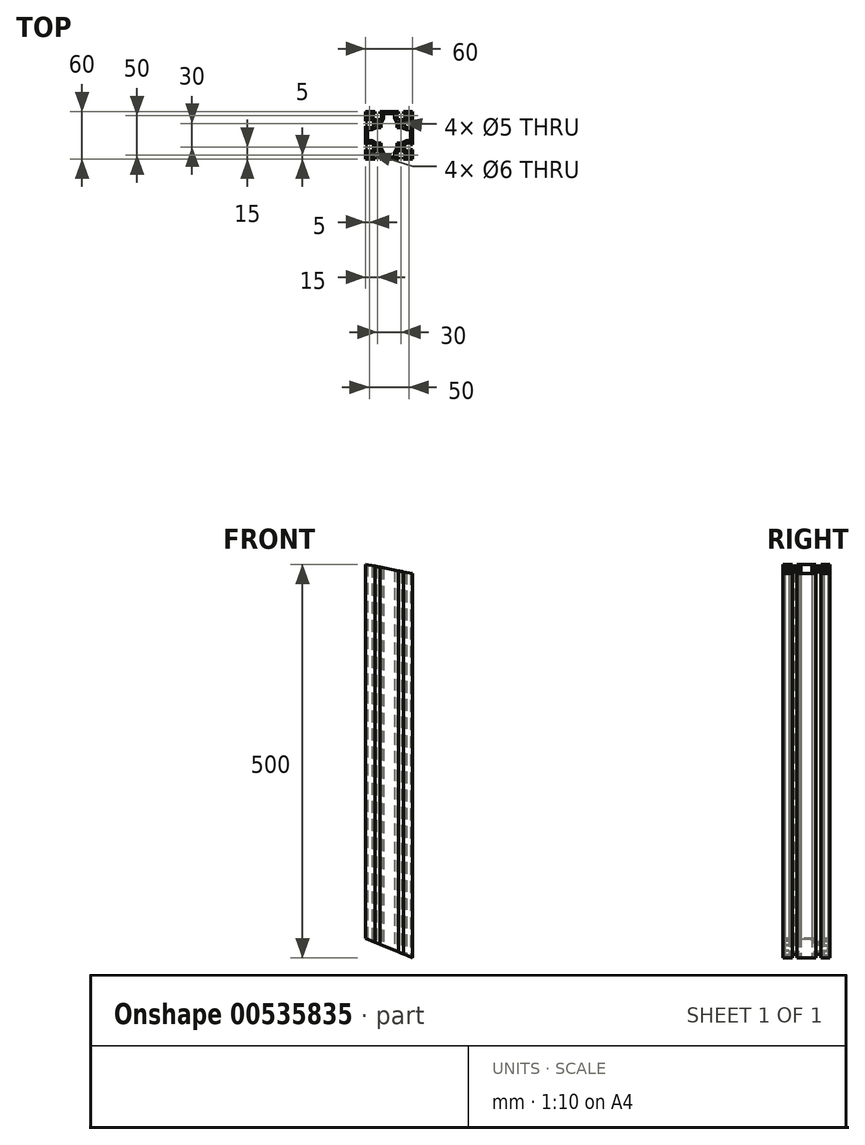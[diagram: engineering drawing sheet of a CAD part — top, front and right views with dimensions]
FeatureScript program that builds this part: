
annotation { "Feature Type Name" : "Feature", "Feature Type Description" : "" }
export const myFeature = defineFeature(function(context is Context, id is Id, definition is map)
    precondition{}
    {
        {
            var Q0;
            Q0=qCreatedBy(makeId("Top.planeOp"),FACE);
            var sketch = newSketch(context, id + "F0", { "sketchPlane" : qUnion([Q0])});
            skLineSegment(sketch, "E0.bottom", {"start": v(30, -30) * mm, "end": v(-30, -30) * mm});
            skLineSegment(sketch, "E0.top", {"start": v(30, 30) * mm, "end": v(-30, 30) * mm});
            skLineSegment(sketch, "E0.left", {"start": v(30, -30) * mm, "end": v(30, 30) * mm});
            skLineSegment(sketch, "E0.right", {"start": v(-30, -30) * mm, "end": v(-30, 30) * mm});
            skPoint(sketch, "E0.middle", {"position": v(0, 0) * mm});
            skLineSegment(sketch, "E1.top", {"start": v(-11.85, 30) * mm, "end": v(-18.15, 30) * mm});
            skLineSegment(sketch, "E1.left", {"start": v(-11.85, 27.5) * mm, "end": v(-11.85, 30) * mm});
            skLineSegment(sketch, "E1.right", {"start": v(-18.15, 27.5) * mm, "end": v(-18.15, 30) * mm});
            skPoint(sketch, "E1.middle", {"position": v(-15, 28.75) * mm});
            skLineSegment(sketch, "E2.bottom", {"start": v(-9.85, 27.5) * mm, "end": v(-11.85, 27.5) * mm});
            skLineSegment(sketch, "E2.left", {"start": v(-9.85, 27.5) * mm, "end": v(-9.85, 21.55) * mm});
            skLineSegment(sketch, "E2.right", {"start": v(-20.15, 27.5) * mm, "end": v(-20.15, 21.55) * mm});
            skPoint(sketch, "E2.middle", {"position": v(-15, 24.52) * mm});
            skArc(sketch, "E3", {"start": v(-20.15, 21.55) * mm, "mid": v(-15, 19.5) * mm, "end": v(-9.85, 21.55) * mm});
            skPoint(sketch, "E4.MirrorP", {"position": v(15, 24.52) * mm});
            skPoint(sketch, "E5.MirrorP", {"position": v(15, 28.75) * mm});
            skLineSegment(sketch, "E6.MirrorCS", {"start": v(11.85, 27.5) * mm, "end": v(11.85, 30) * mm});
            skLineSegment(sketch, "E7.MirrorCS", {"start": v(18.15, 27.5) * mm, "end": v(18.15, 30) * mm});
            skLineSegment(sketch, "E8.MirrorCS", {"start": v(9.85, 27.5) * mm, "end": v(11.85, 27.5) * mm});
            skLineSegment(sketch, "E9.MirrorCS", {"start": v(9.85, 27.5) * mm, "end": v(9.85, 21.55) * mm});
            skArc(sketch, "E10.MirrorCS", {"start": v(20.15, 21.55) * mm, "mid": v(15, 19.5) * mm, "end": v(9.85, 21.55) * mm});
            skLineSegment(sketch, "E11.MirrorCS", {"start": v(20.15, 27.5) * mm, "end": v(20.15, 21.55) * mm});
            skLineSegment(sketch, "E12.MirrorCS", {"start": v(11.85, 30) * mm, "end": v(18.15, 30) * mm});
            skLineSegment(sketch, "E13.1.0", {"start": v(27.5, 20.15) * mm, "end": v(21.55, 20.15) * mm});
            skLineSegment(sketch, "E13.1.1", {"start": v(27.5, 9.85) * mm, "end": v(21.55, 9.85) * mm});
            skArc(sketch, "E13.1.2", {"start": v(21.55, 20.15) * mm, "mid": v(19.5, 15) * mm, "end": v(21.55, 9.85) * mm});
            skLineSegment(sketch, "E13.1.3", {"start": v(27.5, -9.85) * mm, "end": v(21.55, -9.85) * mm});
            skLineSegment(sketch, "E13.1.4", {"start": v(27.5, -20.15) * mm, "end": v(21.55, -20.15) * mm});
            skPoint(sketch, "E13.1.5", {"position": v(28.75, 15) * mm});
            skPoint(sketch, "E13.1.6", {"position": v(28.75, -15) * mm});
            skArc(sketch, "E13.1.7", {"start": v(21.55, -20.15) * mm, "mid": v(19.5, -15) * mm, "end": v(21.55, -9.85) * mm});
            skPoint(sketch, "E13.1.8", {"position": v(24.52, -15) * mm});
            skPoint(sketch, "E13.1.9", {"position": v(24.52, 15) * mm});
            skLineSegment(sketch, "E13.1.10", {"start": v(27.5, 9.85) * mm, "end": v(27.5, 20.15) * mm});
            skLineSegment(sketch, "E13.1.11", {"start": v(27.5, -11.85) * mm, "end": v(27.5, -18.15) * mm});
            skLineSegment(sketch, "E13.1.12", {"start": v(30, 11.85) * mm, "end": v(30, 18.15) * mm});
            skLineSegment(sketch, "E13.1.13", {"start": v(30, -11.85) * mm, "end": v(30, -18.15) * mm});
            skLineSegment(sketch, "E13.1.14", {"start": v(27.5, 18.15) * mm, "end": v(30, 18.15) * mm});
            skLineSegment(sketch, "E13.1.15", {"start": v(27.5, 11.85) * mm, "end": v(30, 11.85) * mm});
            skLineSegment(sketch, "E13.1.16", {"start": v(27.5, 11.85) * mm, "end": v(27.5, 18.15) * mm});
            skLineSegment(sketch, "E13.1.17", {"start": v(27.5, -9.85) * mm, "end": v(27.5, -20.15) * mm});
            skLineSegment(sketch, "E13.1.18", {"start": v(27.5, -18.15) * mm, "end": v(30, -18.15) * mm});
            skLineSegment(sketch, "E13.1.19", {"start": v(27.5, -11.85) * mm, "end": v(30, -11.85) * mm});
            skLineSegment(sketch, "E13.2.0", {"start": v(20.15, -27.5) * mm, "end": v(20.15, -21.55) * mm});
            skLineSegment(sketch, "E13.2.1", {"start": v(9.85, -27.5) * mm, "end": v(9.85, -21.55) * mm});
            skArc(sketch, "E13.2.2", {"start": v(20.15, -21.55) * mm, "mid": v(15, -19.5) * mm, "end": v(9.85, -21.55) * mm});
            skLineSegment(sketch, "E13.2.3", {"start": v(-9.85, -27.5) * mm, "end": v(-9.85, -21.55) * mm});
            skLineSegment(sketch, "E13.2.4", {"start": v(-20.15, -27.5) * mm, "end": v(-20.15, -21.55) * mm});
            skPoint(sketch, "E13.2.5", {"position": v(15, -28.75) * mm});
            skPoint(sketch, "E13.2.6", {"position": v(-15, -28.75) * mm});
            skArc(sketch, "E13.2.7", {"start": v(-20.15, -21.55) * mm, "mid": v(-15, -19.5) * mm, "end": v(-9.85, -21.55) * mm});
            skPoint(sketch, "E13.2.8", {"position": v(-15, -24.52) * mm});
            skPoint(sketch, "E13.2.9", {"position": v(15, -24.52) * mm});
            skLineSegment(sketch, "E13.2.10", {"start": v(9.85, -27.5) * mm, "end": v(20.15, -27.5) * mm});
            skLineSegment(sketch, "E13.2.11", {"start": v(-11.85, -27.5) * mm, "end": v(-18.15, -27.5) * mm});
            skLineSegment(sketch, "E13.2.12", {"start": v(11.85, -30) * mm, "end": v(18.15, -30) * mm});
            skLineSegment(sketch, "E13.2.13", {"start": v(-11.85, -30) * mm, "end": v(-18.15, -30) * mm});
            skLineSegment(sketch, "E13.2.14", {"start": v(18.15, -27.5) * mm, "end": v(18.15, -30) * mm});
            skLineSegment(sketch, "E13.2.15", {"start": v(11.85, -27.5) * mm, "end": v(11.85, -30) * mm});
            skLineSegment(sketch, "E13.2.16", {"start": v(11.85, -27.5) * mm, "end": v(18.15, -27.5) * mm});
            skLineSegment(sketch, "E13.2.17", {"start": v(-9.85, -27.5) * mm, "end": v(-20.15, -27.5) * mm});
            skLineSegment(sketch, "E13.2.18", {"start": v(-18.15, -27.5) * mm, "end": v(-18.15, -30) * mm});
            skLineSegment(sketch, "E13.2.19", {"start": v(-11.85, -27.5) * mm, "end": v(-11.85, -30) * mm});
            skLineSegment(sketch, "E13.3.0", {"start": v(-27.5, -20.15) * mm, "end": v(-21.55, -20.15) * mm});
            skLineSegment(sketch, "E13.3.1", {"start": v(-27.5, -9.85) * mm, "end": v(-21.55, -9.85) * mm});
            skArc(sketch, "E13.3.2", {"start": v(-21.55, -20.15) * mm, "mid": v(-19.5, -15) * mm, "end": v(-21.55, -9.85) * mm});
            skLineSegment(sketch, "E13.3.3", {"start": v(-27.5, 9.85) * mm, "end": v(-21.55, 9.85) * mm});
            skLineSegment(sketch, "E13.3.4", {"start": v(-27.5, 20.15) * mm, "end": v(-21.55, 20.15) * mm});
            skPoint(sketch, "E13.3.5", {"position": v(-28.75, -15) * mm});
            skPoint(sketch, "E13.3.6", {"position": v(-28.75, 15) * mm});
            skArc(sketch, "E13.3.7", {"start": v(-21.55, 20.15) * mm, "mid": v(-19.5, 15) * mm, "end": v(-21.55, 9.85) * mm});
            skPoint(sketch, "E13.3.8", {"position": v(-24.52, 15) * mm});
            skPoint(sketch, "E13.3.9", {"position": v(-24.52, -15) * mm});
            skLineSegment(sketch, "E13.3.10", {"start": v(-27.5, -9.85) * mm, "end": v(-27.5, -20.15) * mm});
            skLineSegment(sketch, "E13.3.11", {"start": v(-27.5, 11.85) * mm, "end": v(-27.5, 18.15) * mm});
            skLineSegment(sketch, "E13.3.12", {"start": v(-30, -11.85) * mm, "end": v(-30, -18.15) * mm});
            skLineSegment(sketch, "E13.3.13", {"start": v(-30, 11.85) * mm, "end": v(-30, 18.15) * mm});
            skLineSegment(sketch, "E13.3.14", {"start": v(-27.5, -18.15) * mm, "end": v(-30, -18.15) * mm});
            skLineSegment(sketch, "E13.3.15", {"start": v(-27.5, -11.85) * mm, "end": v(-30, -11.85) * mm});
            skLineSegment(sketch, "E13.3.16", {"start": v(-27.5, -11.85) * mm, "end": v(-27.5, -18.15) * mm});
            skLineSegment(sketch, "E13.3.17", {"start": v(-27.5, 9.85) * mm, "end": v(-27.5, 20.15) * mm});
            skLineSegment(sketch, "E13.3.18", {"start": v(-27.5, 18.15) * mm, "end": v(-30, 18.15) * mm});
            skLineSegment(sketch, "E13.3.19", {"start": v(-27.5, 11.85) * mm, "end": v(-30, 11.85) * mm});
            skLineSegment(sketch, "E13.anchor1", {"start": v(0, 0) * mm, "end": v(-20.15, 21.55) * mm, "construction": true});
            skLineSegment(sketch, "E13.anchor2", {"start": v(0, 0) * mm, "end": v(-21.55, -20.15) * mm, "construction": true});
            skLineSegment(sketch, "E14.trimOffspring", {"start": v(-18.15, 27.5) * mm, "end": v(-20.15, 27.5) * mm});
            skLineSegment(sketch, "E15.trimOffspring", {"start": v(18.15, 27.5) * mm, "end": v(20.15, 27.5) * mm});
            skCircle(sketch, "E16", {"center": v(-15, 15) * mm, "radius": 2.5 * mm});
            skCircle(sketch, "E17", {"center": v(-25, 25) * mm, "radius": 3 * mm});
            skCircle(sketch, "E18.MirrorC", {"center": v(25, 25) * mm, "radius": 3 * mm});
            skCircle(sketch, "E19.MirrorC", {"center": v(25, -25) * mm, "radius": 3 * mm});
            skCircle(sketch, "E20.MirrorC", {"center": v(-25, -25) * mm, "radius": 3 * mm});
            skCircle(sketch, "E21.MirrorC", {"center": v(15, 15) * mm, "radius": 2.5 * mm});
            skCircle(sketch, "E22.MirrorC", {"center": v(15, -15) * mm, "radius": 2.5 * mm});
            skCircle(sketch, "E23.MirrorC", {"center": v(-15, -15) * mm, "radius": 2.5 * mm});
            skLineSegment(sketch, "E24", {"start": v(-7, 27.5) * mm, "end": v(0, 27.5) * mm});
            skLineSegment(sketch, "E25", {"start": v(-7, 27.5) * mm, "end": v(-7, 22) * mm});
            skLineSegment(sketch, "E26", {"start": v(-10, 10) * mm, "end": v(-10, 16) * mm});
            skLineSegment(sketch, "E27", {"start": v(-10, 16) * mm, "end": v(-7, 22) * mm});
            skLineSegment(sketch, "E28.MirrorCS", {"start": v(10, 10) * mm, "end": v(10, 16) * mm});
            skLineSegment(sketch, "E29.MirrorCS", {"start": v(10, 16) * mm, "end": v(7, 22) * mm});
            skLineSegment(sketch, "E30.MirrorCS", {"start": v(7, 27.5) * mm, "end": v(0, 27.5) * mm});
            skLineSegment(sketch, "E31.MirrorCS", {"start": v(7, 27.5) * mm, "end": v(7, 22) * mm});
            skLineSegment(sketch, "E32.1.0", {"start": v(-10, -10) * mm, "end": v(-16, -10) * mm});
            skLineSegment(sketch, "E32.1.1", {"start": v(-16, -10) * mm, "end": v(-22, -7) * mm});
            skLineSegment(sketch, "E32.1.2", {"start": v(-27.5, -7) * mm, "end": v(-22, -7) * mm});
            skLineSegment(sketch, "E32.1.3", {"start": v(-27.5, -7) * mm, "end": v(-27.5, 0) * mm});
            skLineSegment(sketch, "E32.1.4", {"start": v(-27.5, 7) * mm, "end": v(-27.5, 0) * mm});
            skLineSegment(sketch, "E32.1.5", {"start": v(-27.5, 7) * mm, "end": v(-22, 7) * mm});
            skLineSegment(sketch, "E32.1.6", {"start": v(-16, 10) * mm, "end": v(-22, 7) * mm});
            skLineSegment(sketch, "E32.1.7", {"start": v(-10, 10) * mm, "end": v(-16, 10) * mm});
            skLineSegment(sketch, "E32.2.0", {"start": v(10, -10) * mm, "end": v(10, -16) * mm});
            skLineSegment(sketch, "E32.2.1", {"start": v(10, -16) * mm, "end": v(7, -22) * mm});
            skLineSegment(sketch, "E32.2.2", {"start": v(7, -27.5) * mm, "end": v(7, -22) * mm});
            skLineSegment(sketch, "E32.2.3", {"start": v(7, -27.5) * mm, "end": v(0, -27.5) * mm});
            skLineSegment(sketch, "E32.2.4", {"start": v(-7, -27.5) * mm, "end": v(0, -27.5) * mm});
            skLineSegment(sketch, "E32.2.5", {"start": v(-7, -27.5) * mm, "end": v(-7, -22) * mm});
            skLineSegment(sketch, "E32.2.6", {"start": v(-10, -16) * mm, "end": v(-7, -22) * mm});
            skLineSegment(sketch, "E32.2.7", {"start": v(-10, -10) * mm, "end": v(-10, -16) * mm});
            skLineSegment(sketch, "E32.3.0", {"start": v(10, 10) * mm, "end": v(16, 10) * mm});
            skLineSegment(sketch, "E32.3.1", {"start": v(16, 10) * mm, "end": v(22, 7) * mm});
            skLineSegment(sketch, "E32.3.2", {"start": v(27.5, 7) * mm, "end": v(22, 7) * mm});
            skLineSegment(sketch, "E32.3.3", {"start": v(27.5, 7) * mm, "end": v(27.5, 0) * mm});
            skLineSegment(sketch, "E32.3.4", {"start": v(27.5, -7) * mm, "end": v(27.5, 0) * mm});
            skLineSegment(sketch, "E32.3.5", {"start": v(27.5, -7) * mm, "end": v(22, -7) * mm});
            skLineSegment(sketch, "E32.3.6", {"start": v(16, -10) * mm, "end": v(22, -7) * mm});
            skLineSegment(sketch, "E32.3.7", {"start": v(10, -10) * mm, "end": v(16, -10) * mm});
            skSolve(sketch);
        }
        {
            var Q0;
            {var subQ30=sQuery(id+"F0.wireOp",EDGE,"E1.left");Q0=makeQuery(id+"F0.imprint","IMPRINT",FACE,{"disambiguationData":[TD([[makeQuery(id+"F0.imprint","IMPRINT",EDGE,{"derivedFrom":subQ30}),-1.0]])]});}
            extrude(context, id + "F1", {"entities" : qUnion([Q0]), "depth" : 500 * mm, "offsetDistance" : 25 * mm});
        }
        {
            var Q0;
            Q0=makeQuery(id+"F1.opExtrude","SWEPT_EDGE",EDGE,{"disambiguationData":[OSD([sQuery(id+"F0.wireOp",EDGE,"E24"),sQuery(id+"F0.wireOp",EDGE,"E25")])]});
            var Q1;
            Q1=makeQuery(id+"F1.opExtrude","SWEPT_EDGE",EDGE,{"disambiguationData":[OSD([sQuery(id+"F0.wireOp",EDGE,"E30.MirrorCS"),sQuery(id+"F0.wireOp",EDGE,"E31.MirrorCS")])]});
            var Q2;
            Q2=makeQuery(id+"F1.opExtrude","SWEPT_EDGE",EDGE,{"disambiguationData":[OSD([sQuery(id+"F0.wireOp",EDGE,"840db5bc-c403-45cd-90c7-254e62d9e8c5.3.2"),sQuery(id+"F0.wireOp",EDGE,"840db5bc-c403-45cd-90c7-254e62d9e8c5.3.3")])]});
            var Q3;
            Q3=makeQuery(id+"F1.opExtrude","SWEPT_EDGE",EDGE,{"disambiguationData":[OSD([sQuery(id+"F0.wireOp",EDGE,"840db5bc-c403-45cd-90c7-254e62d9e8c5.3.4"),sQuery(id+"F0.wireOp",EDGE,"840db5bc-c403-45cd-90c7-254e62d9e8c5.3.5")])]});
            var Q4;
            Q4=makeQuery(id+"F1.opExtrude","SWEPT_EDGE",EDGE,{"disambiguationData":[OSD([sQuery(id+"F0.wireOp",EDGE,"840db5bc-c403-45cd-90c7-254e62d9e8c5.1.4"),sQuery(id+"F0.wireOp",EDGE,"840db5bc-c403-45cd-90c7-254e62d9e8c5.1.5")])]});
            var Q5;
            Q5=makeQuery(id+"F1.opExtrude","SWEPT_EDGE",EDGE,{"disambiguationData":[OSD([sQuery(id+"F0.wireOp",EDGE,"840db5bc-c403-45cd-90c7-254e62d9e8c5.1.2"),sQuery(id+"F0.wireOp",EDGE,"840db5bc-c403-45cd-90c7-254e62d9e8c5.1.3")])]});
            var Q6;
            Q6=makeQuery(id+"F1.opExtrude","SWEPT_EDGE",EDGE,{"disambiguationData":[OSD([sQuery(id+"F0.wireOp",EDGE,"840db5bc-c403-45cd-90c7-254e62d9e8c5.2.2"),sQuery(id+"F0.wireOp",EDGE,"840db5bc-c403-45cd-90c7-254e62d9e8c5.2.3")])]});
            var Q7;
            Q7=makeQuery(id+"F1.opExtrude","SWEPT_EDGE",EDGE,{"disambiguationData":[OSD([sQuery(id+"F0.wireOp",EDGE,"840db5bc-c403-45cd-90c7-254e62d9e8c5.2.4"),sQuery(id+"F0.wireOp",EDGE,"840db5bc-c403-45cd-90c7-254e62d9e8c5.2.5")])]});
            fillet(context, id + "F2", {"entities" : qUnion([Q0, Q1, Q2, Q3, Q4, Q5, Q6, Q7]), "radius" : 2 * mm, "tangentPropagation" : true, "allowEdgeOverflow" : false});
        }
        {
            var Q0;
            Q0=makeQuery(id+"F1.opExtrude","SWEPT_EDGE",EDGE,{"disambiguationData":[OSD([sQuery(id+"F0.wireOp",EDGE,"E26"),sQuery(id+"F0.wireOp",EDGE,"E27")])]});
            var Q1;
            Q1=makeQuery(id+"F1.opExtrude","SWEPT_EDGE",EDGE,{"disambiguationData":[OSD([sQuery(id+"F0.wireOp",EDGE,"E28.MirrorCS"),sQuery(id+"F0.wireOp",EDGE,"E29.MirrorCS")])]});
            var Q2;
            Q2=makeQuery(id+"F1.opExtrude","SWEPT_EDGE",EDGE,{"disambiguationData":[OSD([sQuery(id+"F0.wireOp",EDGE,"840db5bc-c403-45cd-90c7-254e62d9e8c5.3.0"),sQuery(id+"F0.wireOp",EDGE,"840db5bc-c403-45cd-90c7-254e62d9e8c5.3.1")])]});
            var Q3;
            Q3=makeQuery(id+"F1.opExtrude","SWEPT_EDGE",EDGE,{"disambiguationData":[OSD([sQuery(id+"F0.wireOp",EDGE,"840db5bc-c403-45cd-90c7-254e62d9e8c5.1.6"),sQuery(id+"F0.wireOp",EDGE,"840db5bc-c403-45cd-90c7-254e62d9e8c5.1.7")])]});
            var Q4;
            Q4=makeQuery(id+"F1.opExtrude","SWEPT_EDGE",EDGE,{"disambiguationData":[OSD([sQuery(id+"F0.wireOp",EDGE,"840db5bc-c403-45cd-90c7-254e62d9e8c5.1.0"),sQuery(id+"F0.wireOp",EDGE,"840db5bc-c403-45cd-90c7-254e62d9e8c5.1.1")])]});
            var Q5;
            Q5=makeQuery(id+"F1.opExtrude","SWEPT_EDGE",EDGE,{"disambiguationData":[OSD([sQuery(id+"F0.wireOp",EDGE,"840db5bc-c403-45cd-90c7-254e62d9e8c5.3.6"),sQuery(id+"F0.wireOp",EDGE,"840db5bc-c403-45cd-90c7-254e62d9e8c5.3.7")])]});
            var Q6;
            Q6=makeQuery(id+"F1.opExtrude","SWEPT_EDGE",EDGE,{"disambiguationData":[OSD([sQuery(id+"F0.wireOp",EDGE,"840db5bc-c403-45cd-90c7-254e62d9e8c5.2.0"),sQuery(id+"F0.wireOp",EDGE,"840db5bc-c403-45cd-90c7-254e62d9e8c5.2.1")])]});
            var Q7;
            Q7=makeQuery(id+"F1.opExtrude","SWEPT_EDGE",EDGE,{"disambiguationData":[OSD([sQuery(id+"F0.wireOp",EDGE,"840db5bc-c403-45cd-90c7-254e62d9e8c5.2.6"),sQuery(id+"F0.wireOp",EDGE,"840db5bc-c403-45cd-90c7-254e62d9e8c5.2.7")])]});
            fillet(context, id + "F3", {"entities" : qUnion([Q0, Q1, Q2, Q3, Q4, Q5, Q6, Q7]), "radius" : 7 * mm, "tangentPropagation" : true, "allowEdgeOverflow" : false});
        }
        {
            var Q0;
            {var subQ0=sQuery(id+"F0.wireOp",EDGE,"E0.bottom");Q0=makeQuery(id+"F1.opExtrude","SWEPT_FACE",FACE,{"disambiguationData":[OSD([subQ0]),TDD([makeQuery(id+"F0.imprint","IMPRINT",EDGE,{"disambiguationData":[TD([[makeQuery(id+"F0.imprint","INTERSECT",VERTEX,{"derivedFrom":[subQ0,sQuery(id+"F0.wireOp",EDGE,"E13.2.12"),sQuery(id+"F0.wireOp",EDGE,"E13.2.15")]}),-1.0]])],"derivedFrom":subQ0})])]});}
            var sketch = newSketch(context, id + "F4", { "sketchPlane" : qUnion([Q0])});
            skLineSegment(sketch, "E33.0", {"start": v(-18.15, 500) * mm, "end": v(-30, 500) * mm});
            skLineSegment(sketch, "E33.1", {"start": v(30, 500) * mm, "end": v(30, 0) * mm});
            skLineSegment(sketch, "E34", {"start": v(-30, 500) * mm, "end": v(30, 500) * mm});
            skLineSegment(sketch, "E35", {"start": v(30, 440) * mm, "end": v(-30, 500) * mm});
            skLineSegment(sketch, "E36.0", {"start": v(-18.15, 0) * mm, "end": v(-30, 0) * mm});
            skLineSegment(sketch, "E37", {"start": v(-30, 0) * mm, "end": v(30, 0) * mm});
            skLineSegment(sketch, "E38", {"start": v(30, 60) * mm, "end": v(-30, 0) * mm});
            skSolve(sketch);
        }
        {
            var Q0;
            Q0=qCreatedBy(makeId("Front.planeOp"),FACE);
            var sketch = newSketch(context, id + "F5", { "sketchPlane" : qUnion([Q0])});
            skLineSegment(sketch, "E39.bottom", {"start": v(10.2, 702.08) * mm, "end": v(190.52, 666.22) * mm});
            skLineSegment(sketch, "E39.top", {"start": v(-30, 500) * mm, "end": v(150.32, 464.13) * mm});
            skLineSegment(sketch, "E39.left", {"start": v(10.2, 702.08) * mm, "end": v(-30, 500) * mm});
            skLineSegment(sketch, "E39.right", {"start": v(190.52, 666.22) * mm, "end": v(150.32, 464.13) * mm});
            skLineSegment(sketch, "E40.bottom", {"start": v(30, 0) * mm, "end": v(-147.62, 73.57) * mm});
            skLineSegment(sketch, "E40.top", {"start": v(-47.9, -188.07) * mm, "end": v(-225.52, -114.5) * mm});
            skLineSegment(sketch, "E40.left", {"start": v(30, 0) * mm, "end": v(-47.9, -188.07) * mm});
            skLineSegment(sketch, "E40.right", {"start": v(-147.62, 73.57) * mm, "end": v(-225.52, -114.5) * mm});
            skSolve(sketch);
        }
        {
            var Q0;
            Q0=makeQuery(id+"F5.imprint","IMPRINT",FACE,{"disambiguationData":[TD([[makeQuery(id+"F5.imprint","IMPRINT",EDGE,{"derivedFrom":sQuery(id+"F5.wireOp",EDGE,"E39.bottom")}),-1.0]])]});
            var Q1;
            Q1=makeQuery(id+"F5.imprint","IMPRINT",FACE,{"disambiguationData":[TD([[makeQuery(id+"F5.imprint","IMPRINT",EDGE,{"derivedFrom":sQuery(id+"F5.wireOp",EDGE,"E40.bottom")}),1.0]])]});
            extrude(context, id + "F6", {"entities" : qUnion([Q0, Q1]), "operationType" : NewBodyOperationType.REMOVE, "depth" : 30 * mm, "offsetDistance" : 25 * mm, "hasSecondDirection" : true, "secondDirectionOppositeDirection" : true, "secondDirectionDepth" : 30 * mm});
        }
    });
